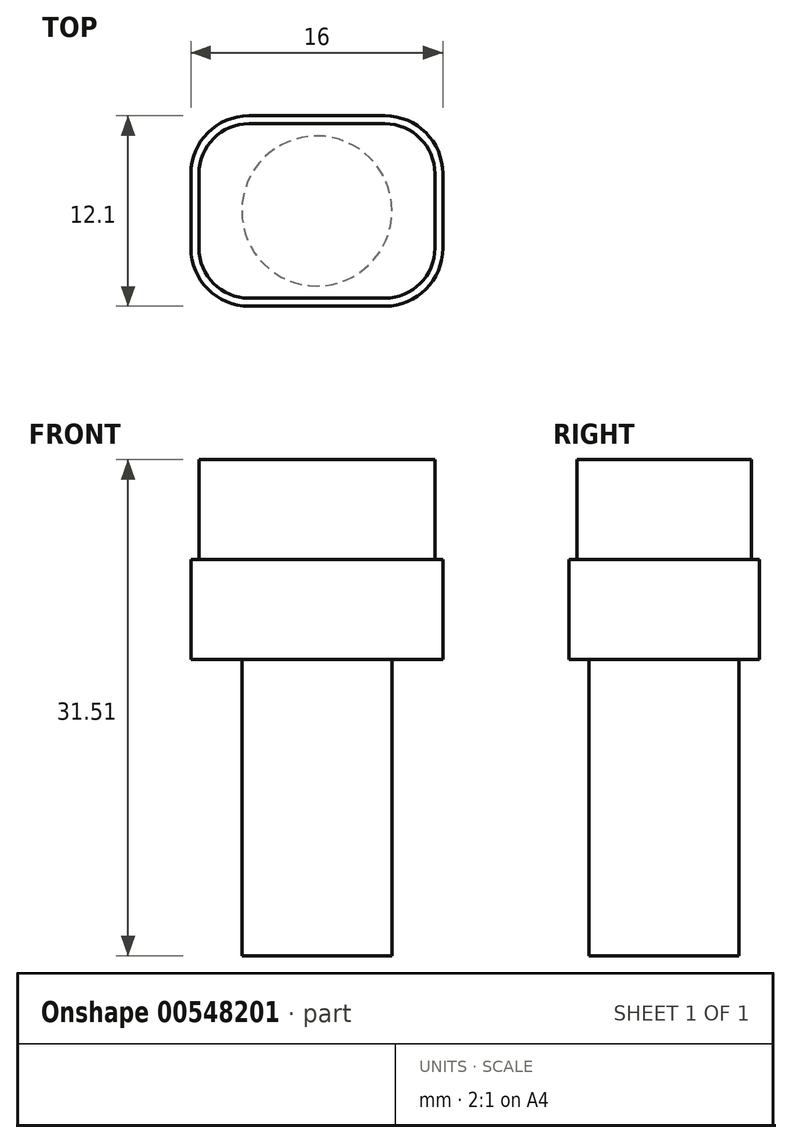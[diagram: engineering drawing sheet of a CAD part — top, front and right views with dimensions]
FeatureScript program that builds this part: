
annotation { "Feature Type Name" : "Feature", "Feature Type Description" : "" }
export const myFeature = defineFeature(function(context is Context, id is Id, definition is map)
    precondition{}
    {
        {
            var Q0;
            Q0=qCreatedBy(makeId("Top.planeOp"),FACE);
            var sketch = newSketch(context, id + "F0", { "sketchPlane" : qUnion([Q0])});
            skCircle(sketch, "E0", {"center": v(0, 0) * mm, "radius": 4.76 * mm});
            skSolve(sketch);
        }
        {
            var Q0;
            Q0=qSketchRegion(id+"F0",true);
            extrude(context, id + "F1", {"entities" : qUnion([Q0]), "depth" : 18.8 * mm, "offsetDistance" : 25.4 * mm});
        }
        {
            var Q0;
            Q0=makeQuery(id+"F1.opExtrude","CAP_FACE",FACE,{"disambiguationData":[OSD([sQuery(id+"F0.wireOp",EDGE,"E0")])],"isStart":false});
            var sketch = newSketch(context, id + "F2", { "sketchPlane" : qUnion([Q0])});
            skLineSegment(sketch, "E1.bottom", {"start": v(4.32, 5.54) * mm, "end": v(-4.32, 5.54) * mm});
            skLineSegment(sketch, "E1.top", {"start": v(4.32, -5.54) * mm, "end": v(-4.32, -5.54) * mm});
            skLineSegment(sketch, "E1.left", {"start": v(7.5, 2.36) * mm, "end": v(7.5, -2.36) * mm});
            skLineSegment(sketch, "E1.right", {"start": v(-7.5, 2.36) * mm, "end": v(-7.5, -2.36) * mm});
            skPoint(sketch, "E1.middle", {"position": v(0, 0) * mm});
            skPoint(sketch, "E2.visualSharp", {"position": v(-7.5, 5.54) * mm});
            skArc(sketch, "E2.filletArc", {"start": v(-4.32, 5.54) * mm, "mid": v(-6.56, 4.6) * mm, "end": v(-7.5, 2.36) * mm});
            skPoint(sketch, "E3.visualSharp", {"position": v(-7.5, -5.54) * mm});
            skArc(sketch, "E3.filletArc", {"start": v(-7.5, -2.36) * mm, "mid": v(-6.56, -4.6) * mm, "end": v(-4.32, -5.54) * mm});
            skPoint(sketch, "E4.visualSharp", {"position": v(7.5, -5.54) * mm});
            skArc(sketch, "E4.filletArc", {"start": v(4.32, -5.54) * mm, "mid": v(6.56, -4.6) * mm, "end": v(7.5, -2.36) * mm});
            skPoint(sketch, "E5.visualSharp", {"position": v(7.5, 5.54) * mm});
            skArc(sketch, "E5.filletArc", {"start": v(7.5, 2.36) * mm, "mid": v(6.56, 4.6) * mm, "end": v(4.32, 5.54) * mm});
            skArc(sketch, "E6.0", {"start": v(8, 2.36) * mm, "mid": v(6.92, 4.97) * mm, "end": v(4.32, 6.05) * mm});
            skLineSegment(sketch, "E6.1", {"start": v(4.32, 6.05) * mm, "end": v(-4.32, 6.05) * mm});
            skLineSegment(sketch, "E6.2", {"start": v(8, 2.36) * mm, "end": v(8, -2.36) * mm});
            skArc(sketch, "E6.3", {"start": v(-4.32, 6.05) * mm, "mid": v(-6.92, 4.97) * mm, "end": v(-8, 2.36) * mm});
            skArc(sketch, "E6.4", {"start": v(4.32, -6.05) * mm, "mid": v(6.92, -4.97) * mm, "end": v(8, -2.36) * mm});
            skLineSegment(sketch, "E6.5", {"start": v(4.32, -6.05) * mm, "end": v(-4.32, -6.05) * mm});
            skArc(sketch, "E6.6", {"start": v(-8, -2.36) * mm, "mid": v(-6.92, -4.97) * mm, "end": v(-4.32, -6.05) * mm});
            skLineSegment(sketch, "E6.7", {"start": v(-8, 2.36) * mm, "end": v(-8, -2.36) * mm});
            skSolve(sketch);
        }
        {
            var Q0;
            Q0=makeQuery(id+"F2.imprint","IMPRINT",FACE,{"disambiguationData":[TD([[makeQuery(id+"F2.imprint","IMPRINT",EDGE,{"derivedFrom":sQuery(id+"F2.wireOp",EDGE,"E1.bottom")}),1.0]])]});
            var Q1;
            Q1=makeQuery(id+"F2.imprint","IMPRINT",FACE,{"disambiguationData":[TD([[makeQuery(id+"F2.imprint","IMPRINT",EDGE,{"derivedFrom":makeQuery(id+"F1.opExtrude","CAP_EDGE",EDGE,{"disambiguationData":[OSD([sQuery(id+"F0.wireOp",EDGE,"E0")])],"isStart":false})}),1.0]])]});
            extrude(context, id + "F3", {"entities" : qUnion([Q0, Q1]), "operationType" : NewBodyOperationType.ADD, "depth" : 12.7 * mm, "offsetDistance" : 25.4 * mm});
        }
        {
            var Q0;
            Q0=makeQuery(id+"F2.imprint","IMPRINT",FACE,{"disambiguationData":[TD([[makeQuery(id+"F2.imprint","IMPRINT",EDGE,{"derivedFrom":sQuery(id+"F2.wireOp",EDGE,"E1.bottom")}),-1.0]])]});
            extrude(context, id + "F4", {"entities" : qUnion([Q0]), "operationType" : NewBodyOperationType.ADD, "depth" : 6.35 * mm, "offsetDistance" : 25.4 * mm});
        }
    });
